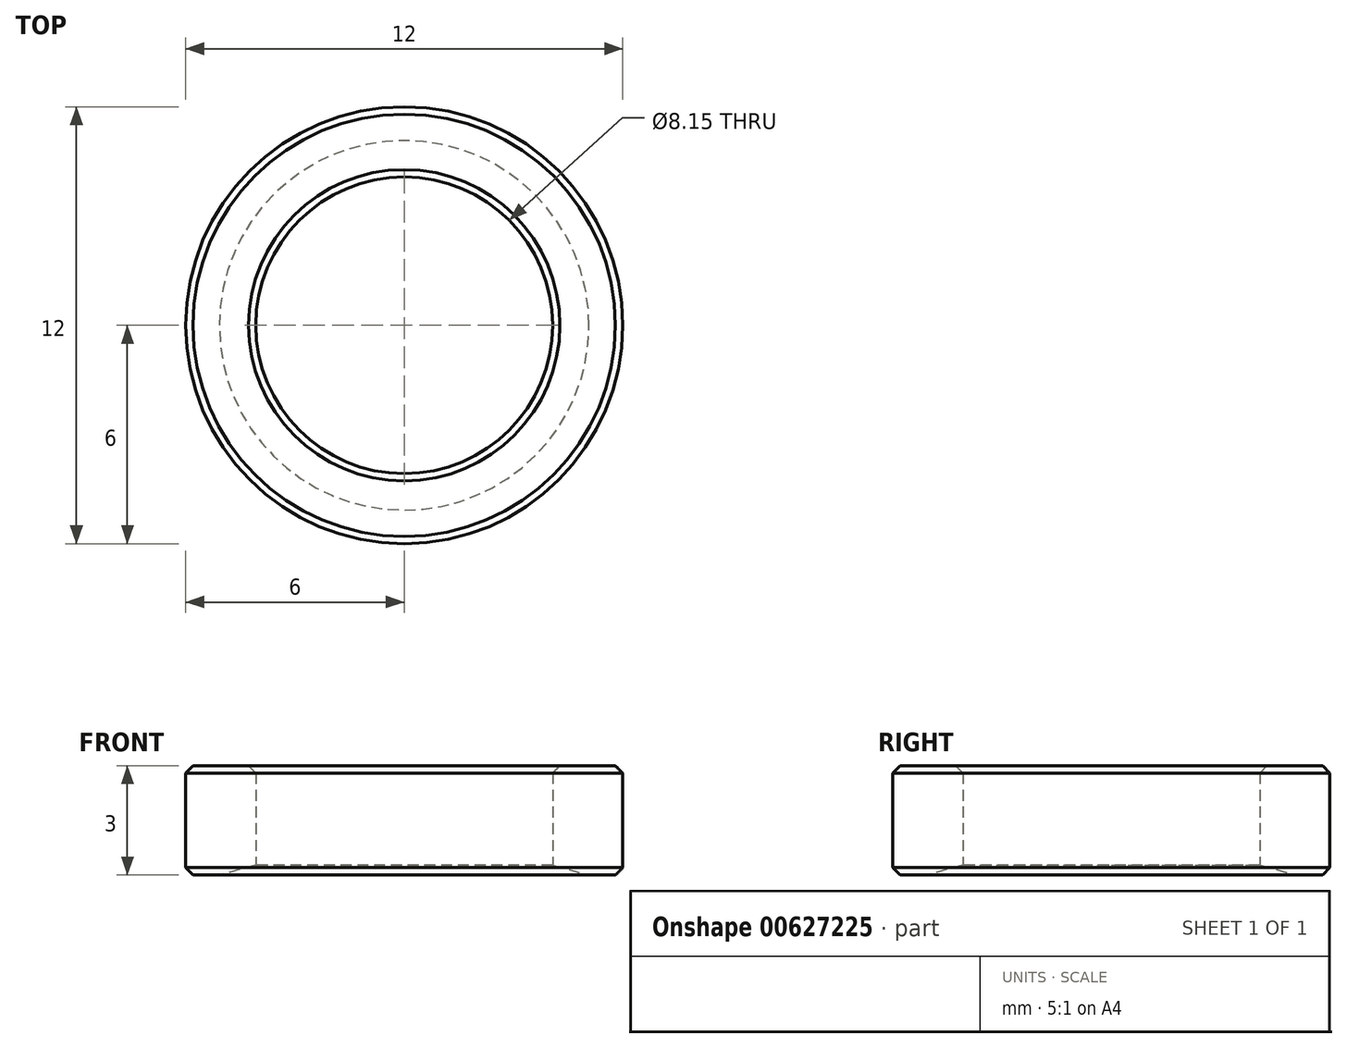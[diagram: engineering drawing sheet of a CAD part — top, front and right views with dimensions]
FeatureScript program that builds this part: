
annotation { "Feature Type Name" : "Feature", "Feature Type Description" : "" }
export const myFeature = defineFeature(function(context is Context, id is Id, definition is map)
    precondition{}
    {
        {
            var Q0;
            Q0=qCreatedBy(makeId("Top.planeOp"),FACE);
            var sketch = newSketch(context, id + "F0", { "sketchPlane" : qUnion([Q0])});
            skCircle(sketch, "E0", {"center": v(0, 0) * mm, "radius": 6 * mm});
            skCircle(sketch, "E1", {"center": v(0, 0) * mm, "radius": 4.08 * mm});
            skSolve(sketch);
        }
        {
            var Q0;
            Q0=makeQuery(id+"F0.imprint","IMPRINT",FACE,{"disambiguationData":[TD([[makeQuery(id+"F0.imprint","IMPRINT",EDGE,{"derivedFrom":sQuery(id+"F0.wireOp",EDGE,"E0")}),1.0]])]});
            extrude(context, id + "F1", {"entities" : qUnion([Q0]), "depth" : 3 * mm, "offsetDistance" : 25 * mm});
        }
        {
            var Q0;
            Q0=makeQuery(id+"F1.opExtrude","CAP_EDGE",EDGE,{"disambiguationData":[OSD([sQuery(id+"F0.wireOp",EDGE,"E1")])],"isStart":false});
            var Q1;
            Q1=makeQuery(id+"F1.opExtrude","CAP_EDGE",EDGE,{"disambiguationData":[OSD([sQuery(id+"F0.wireOp",EDGE,"E0")])],"isStart":true});
            var Q2;
            Q2=makeQuery(id+"F1.opExtrude","CAP_EDGE",EDGE,{"disambiguationData":[OSD([sQuery(id+"F0.wireOp",EDGE,"E0")])],"isStart":false});
            chamfer(context, id + "F2", {"entities" : qUnion([Q0, Q1, Q2]), "width" : 0.2 * mm, "tangentPropagation" : true});
        }
        {
            var Q0;
            Q0=makeQuery(id+"F1.opExtrude","CAP_EDGE",EDGE,{"disambiguationData":[OSD([sQuery(id+"F0.wireOp",EDGE,"E1")])],"isStart":true});
            chamfer(context, id + "F3", {"entities" : qUnion([Q0]), "chamferType" : ChamferType.OFFSET_ANGLE, "width" : 1 * mm, "oppositeDirection" : false, "angle" : 15 * degree, "tangentPropagation" : true});
        }
    });
